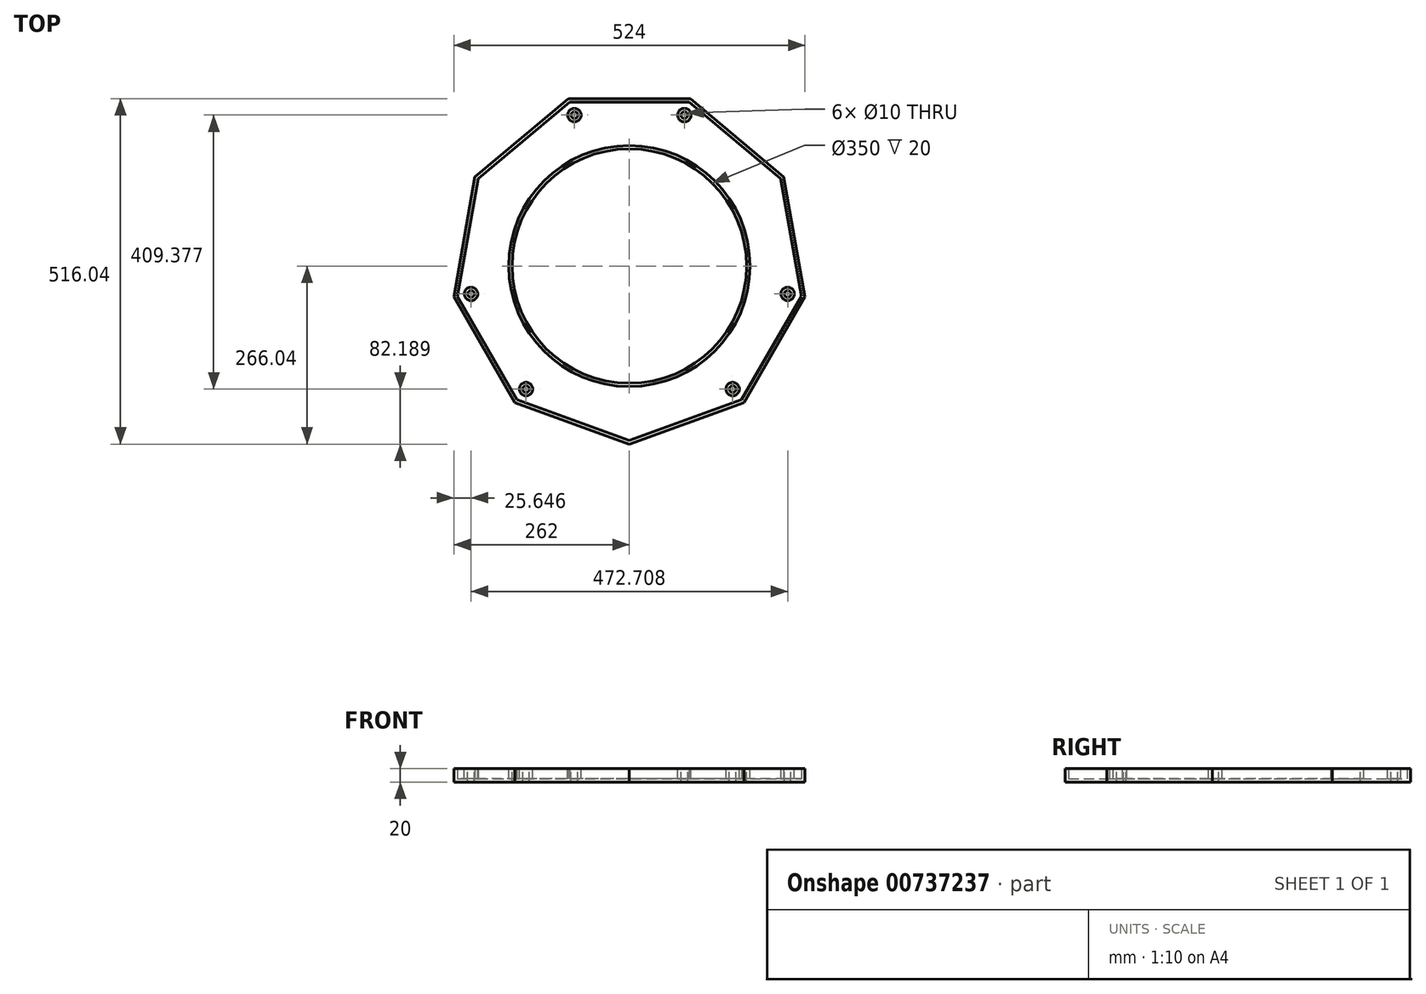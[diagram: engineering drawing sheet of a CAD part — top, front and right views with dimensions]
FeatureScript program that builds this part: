
annotation { "Feature Type Name" : "Feature", "Feature Type Description" : "" }
export const myFeature = defineFeature(function(context is Context, id is Id, definition is map)
    precondition{}
    {
        {
            var Q0;
            Q0=qCreatedBy(makeId("Top.planeOp"),FACE);
            var sketch = newSketch(context, id + "F0", { "sketchPlane" : qUnion([Q0])});
            skCircle(sketch, "E0.cCircle", {"center": v(0, 0) * mm, "radius": 250 * mm, "construction": true});
            skLineSegment(sketch, "E0.0", {"start": v(-91, 250) * mm, "end": v(91, 250) * mm});
            skLineSegment(sketch, "E0.1", {"start": v(91, 250) * mm, "end": v(230.4, 133.02) * mm});
            skLineSegment(sketch, "E0.2", {"start": v(230.4, 133.02) * mm, "end": v(262, -46.2) * mm});
            skLineSegment(sketch, "E0.3", {"start": v(262, -46.2) * mm, "end": v(171.01, -203.8) * mm});
            skLineSegment(sketch, "E0.4", {"start": v(171.01, -203.8) * mm, "end": v(0, -266.04) * mm});
            skLineSegment(sketch, "E0.5", {"start": v(0, -266.04) * mm, "end": v(-171.01, -203.8) * mm});
            skLineSegment(sketch, "E0.6", {"start": v(-171.01, -203.8) * mm, "end": v(-262, -46.2) * mm});
            skLineSegment(sketch, "E0.7", {"start": v(-262, -46.2) * mm, "end": v(-230.4, 133.02) * mm});
            skLineSegment(sketch, "E0.8", {"start": v(-230.4, 133.02) * mm, "end": v(-91, 250) * mm});
            skPoint(sketch, "E0.0.midPoint", {"position": v(0, 250) * mm});
            skSolve(sketch);
        }
        {
            var Q0;
            Q0 = qSketchRegion(id + "F0", true);
            extrude(context, id + "F1", {"entities" : qUnion([Q0]), "depth" : 20 * mm, "offsetDistance" : 25 * mm});
        }
        {
            var Q0;
            Q0=makeQuery(id+"F1.opExtrude","CAP_FACE",FACE,{"disambiguationData":[OSD([sQuery(id+"F0.wireOp",EDGE,"E0.0"),sQuery(id+"F0.wireOp",EDGE,"E0.1"),sQuery(id+"F0.wireOp",EDGE,"E0.2"),sQuery(id+"F0.wireOp",EDGE,"E0.3"),sQuery(id+"F0.wireOp",EDGE,"E0.4"),sQuery(id+"F0.wireOp",EDGE,"E0.5"),sQuery(id+"F0.wireOp",EDGE,"E0.6"),sQuery(id+"F0.wireOp",EDGE,"E0.7"),sQuery(id+"F0.wireOp",EDGE,"E0.8")])],"isStart":false});
            var sketch = newSketch(context, id + "F2", { "sketchPlane" : qUnion([Q0])});
            skCircle(sketch, "E1", {"center": v(0, 0) * mm, "radius": 175 * mm});
            skSolve(sketch);
        }
        {
            var Q0;
            Q0=makeQuery(id+"F2.imprint","IMPRINT",FACE,{"disambiguationData":[TD([[makeQuery(id+"F2.imprint","IMPRINT",EDGE,{"derivedFrom":sQuery(id+"F2.wireOp",EDGE,"E1")}),1.0]])]});
            extrude(context, id + "F3", {"entities" : qUnion([Q0]), "operationType" : NewBodyOperationType.REMOVE, "endBound" : BoundingType.THROUGH_ALL, "oppositeDirection" : true, "depth" : 25 * mm, "offsetDistance" : 25 * mm});
        }
        {
            var Q0;
            Q0=makeQuery(id+"F1.opExtrude","CAP_FACE",FACE,{"disambiguationData":[OSD([sQuery(id+"F0.wireOp",EDGE,"E0.0"),sQuery(id+"F0.wireOp",EDGE,"E0.1"),sQuery(id+"F0.wireOp",EDGE,"E0.2"),sQuery(id+"F0.wireOp",EDGE,"E0.3"),sQuery(id+"F0.wireOp",EDGE,"E0.4"),sQuery(id+"F0.wireOp",EDGE,"E0.5"),sQuery(id+"F0.wireOp",EDGE,"E0.6"),sQuery(id+"F0.wireOp",EDGE,"E0.7"),sQuery(id+"F0.wireOp",EDGE,"E0.8")])],"isStart":false});
            var sketch = newSketch(context, id + "F4", { "sketchPlane" : qUnion([Q0])});
            skCircle(sketch, "E2", {"center": v(-82.08, 225.53) * mm, "radius": 5 * mm});
            skLineSegment(sketch, "E3", {"start": v(0, 0) * mm, "end": v(-91, 250) * mm, "construction": true});
            skLineSegment(sketch, "E4", {"start": v(0, 0) * mm, "end": v(-262, -46.2) * mm, "construction": true});
            skLineSegment(sketch, "E5", {"start": v(0, 0) * mm, "end": v(91, 250) * mm, "construction": true});
            skLineSegment(sketch, "E6", {"start": v(0, 0) * mm, "end": v(262, -46.2) * mm, "construction": true});
            skLineSegment(sketch, "E7", {"start": v(0, 0) * mm, "end": v(-171.01, -203.8) * mm, "construction": true});
            skLineSegment(sketch, "E8", {"start": v(0, 0) * mm, "end": v(171.01, -203.8) * mm, "construction": true});
            skCircle(sketch, "E9.1.0", {"center": v(-154.27, -183.85) * mm, "radius": 5 * mm});
            skCircle(sketch, "E9.2.0", {"center": v(236.35, -41.68) * mm, "radius": 5 * mm});
            skPoint(sketch, "E9.center", {"position": v(0, 0) * mm});
            skCircle(sketch, "E10", {"center": v(82.08, 225.53) * mm, "radius": 5 * mm});
            skCircle(sketch, "E11.1.0", {"center": v(-236.35, -41.68) * mm, "radius": 5 * mm});
            skCircle(sketch, "E11.2.0", {"center": v(154.27, -183.85) * mm, "radius": 5 * mm});
            skSolve(sketch);
        }
        {
            var Q0;
            Q0=makeQuery(id+"F4.imprint","IMPRINT",FACE,{"disambiguationData":[TD([[makeQuery(id+"F4.imprint","IMPRINT",EDGE,{"derivedFrom":sQuery(id+"F4.wireOp",EDGE,"E9.1.0")}),1.0]])]});
            var Q1;
            Q1=makeQuery(id+"F4.imprint","IMPRINT",FACE,{"disambiguationData":[TD([[makeQuery(id+"F4.imprint","IMPRINT",EDGE,{"derivedFrom":sQuery(id+"F4.wireOp",EDGE,"E9.2.0")}),1.0]])]});
            var Q2;
            Q2=makeQuery(id+"F4.imprint","IMPRINT",FACE,{"disambiguationData":[TD([[makeQuery(id+"F4.imprint","IMPRINT",EDGE,{"derivedFrom":sQuery(id+"F4.wireOp",EDGE,"E10")}),1.0]])]});
            var Q3;
            Q3=makeQuery(id+"F4.imprint","IMPRINT",FACE,{"disambiguationData":[TD([[makeQuery(id+"F4.imprint","IMPRINT",EDGE,{"derivedFrom":sQuery(id+"F4.wireOp",EDGE,"E11.1.0")}),1.0]])]});
            var Q4;
            Q4=makeQuery(id+"F4.imprint","IMPRINT",FACE,{"disambiguationData":[TD([[makeQuery(id+"F4.imprint","IMPRINT",EDGE,{"derivedFrom":sQuery(id+"F4.wireOp",EDGE,"E11.2.0")}),1.0]])]});
            var Q5;
            Q5=makeQuery(id+"F4.imprint","IMPRINT",FACE,{"disambiguationData":[TD([[makeQuery(id+"F4.imprint","IMPRINT",EDGE,{"derivedFrom":sQuery(id+"F4.wireOp",EDGE,"E2")}),1.0]])]});
            extrude(context, id + "F5", {"entities" : qUnion([Q0, Q1, Q2, Q3, Q4, Q5]), "operationType" : NewBodyOperationType.REMOVE, "endBound" : BoundingType.THROUGH_ALL, "oppositeDirection" : true, "depth" : 25 * mm, "offsetDistance" : 25 * mm});
        }
        {
            var Q0;
            Q0=makeQuery(id+"F1.opExtrude","CAP_FACE",FACE,{"disambiguationData":[OSD([sQuery(id+"F0.wireOp",EDGE,"E0.0"),sQuery(id+"F0.wireOp",EDGE,"E0.1"),sQuery(id+"F0.wireOp",EDGE,"E0.2"),sQuery(id+"F0.wireOp",EDGE,"E0.3"),sQuery(id+"F0.wireOp",EDGE,"E0.4"),sQuery(id+"F0.wireOp",EDGE,"E0.5"),sQuery(id+"F0.wireOp",EDGE,"E0.6"),sQuery(id+"F0.wireOp",EDGE,"E0.7"),sQuery(id+"F0.wireOp",EDGE,"E0.8")])],"isStart":false});
            shell(context, id + "F6", {"entities" : qUnion([Q0]), "thickness" : 5 * mm});
        }
    });
